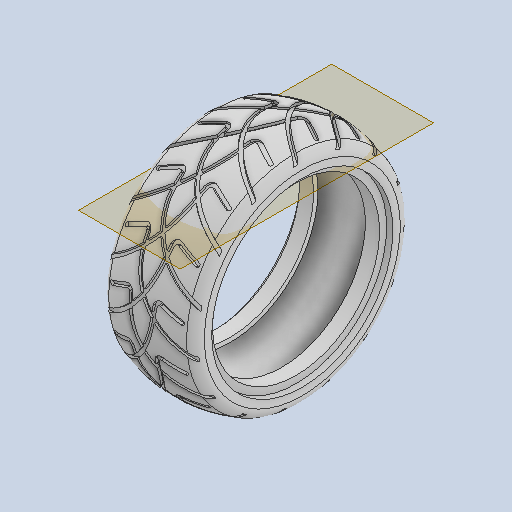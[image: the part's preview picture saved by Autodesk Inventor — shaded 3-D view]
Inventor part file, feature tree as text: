
AUTODESK INVENTOR PART (.ipt)
format: ipt  version: 2024 (Build 280153000, 153)  size: 2,186,240 bytes
history: native  units: in
note: dims shown in document units (in); Inventor stores cm internally (conversion verified against a paired STEP export)
features: sketch x4, revolve x2, other x2, fillet x1, plane x1, extrude x1, pattern_circular x1, mirror x1, direct_edit x1, projected_geometry x1
ambient origin geometry x8: Origin, YZ Plane, XZ Plane, XY Plane, X Axis, Y Axis, Z Axis, Center Point
bodies: Solid1 (feature_tree)
feature tree (15):
  revolve  "Revolution1"  [1 undecoded]
  fillet  "Fillet1"  Radius=0.23in
  plane  "Work Plane1"
  sketch  "Sketch3"  dims[d5=1.045in]
  extrude  "Extrusion1"  Depth=2.6in
  pattern_circular  "Circular Pattern1"  Angle=90.0deg  [1 undecoded]
  mirror  "Mirror1"
  direct_edit  "Direct Edit1"
  sketch  "Sketch1"  dims[d0=1.885in d1=0.07in d2=0.23in]
  sketch  "Sketch2"  dims[d3=2.045in d4=2.6in]
  other  "Srf1"
  sketch  "Sketch4"  dims[d6=0.05in d7=90.0deg d8=0.125in d9=0.0297in d10=90.0deg d11=1.375in d12=0.8744in d13=0.3268in d14=0.765in d15=0.2455in d16=0.0625in d17=0.1044in d18=0.0415in d19=0.1248in d20=0.2825in d21=1.0in d22=0.0in d23=5.9055in d24=360.0deg d26=3.937in d27=0.3937in d28=0.3937in]
  revolve  "RevolutionSrf1"  [1 undecoded]
  projected_geometry  "Project Cut Edges1"
  other  "Scale1"
note: 3 required parameter values undecoded (feature->parameter linkage not recoverable at this tier; creation-order binding heuristic only, values carry confidence <= 0.55)